# Revit family: LCT
name_source: partatom
category: Lighting Fixtures
revit_build: Autodesk Revit 2014 (Build: 20130308_1515(x64)
units: mm (PartAtom-declared; Revit-internal decimal feet)

## types (8) — shared parameters
Apparent Load = 8 VA
Assembly Code = D5020200
Color Filter = 16777215
Connector Description = Lighting Connector
Default Elevation = 48"
Description = Security Lighting's Triangle Pendant offers a dramatic impact in all of today’s contemporary decors.
Dimming Lamp Color Temperature Shift = <None>
Drum-Height = 24"
Emit Shape Visible in Rendering = No
Emit from Circle Diameter = 28"
Features = Engineered to suit all high traffic areas in demanding restaurant environments
White interior color provides glowing effect
Custom shapes, sizes, and colors available
Fixture distribution = Direct
LF = CT : P
Lamp = LED
Load Classification = Lighting
Manufacturer = Security Lighting
Model = LCT
Photometric Web File = generic
Power Factor = 1
Product Documentation Link = https://hubbellcdn.com
Product Link = https://www.hubbell.com
Reflector Finish = Hubbell - White Glass
Tilt Angle = 60.00°
URL = https://www.hubbell.com
Voltage = 120 V
Warranty = 5 years Warranty
Wattage Comments = 8W
Watts = 8 W

## per-type parameters (varying)
| type | Housing Material |
| LCT-P-OO | Paint - Hubbell - Matte White |
| LCT-P-YO | Hubbell - Yellow |
| LCT-P-CG | Paint - Hubbell - Gray Smooth |
| LCT-P-WB | Hubbell - Warm Brown |
| LCT-P-RD | Hubbell - Red |
| LCT-P-GN | Paint - Hubbell - Green Textured |
| LCT-P-OR | Hubbell - Orange |
| LCT-P-BL | Hubbell - Blue |

## geometry (parser evidence)
native form markers: Blend x19, Sweep x3
no freeform markers — native parametric forms only
